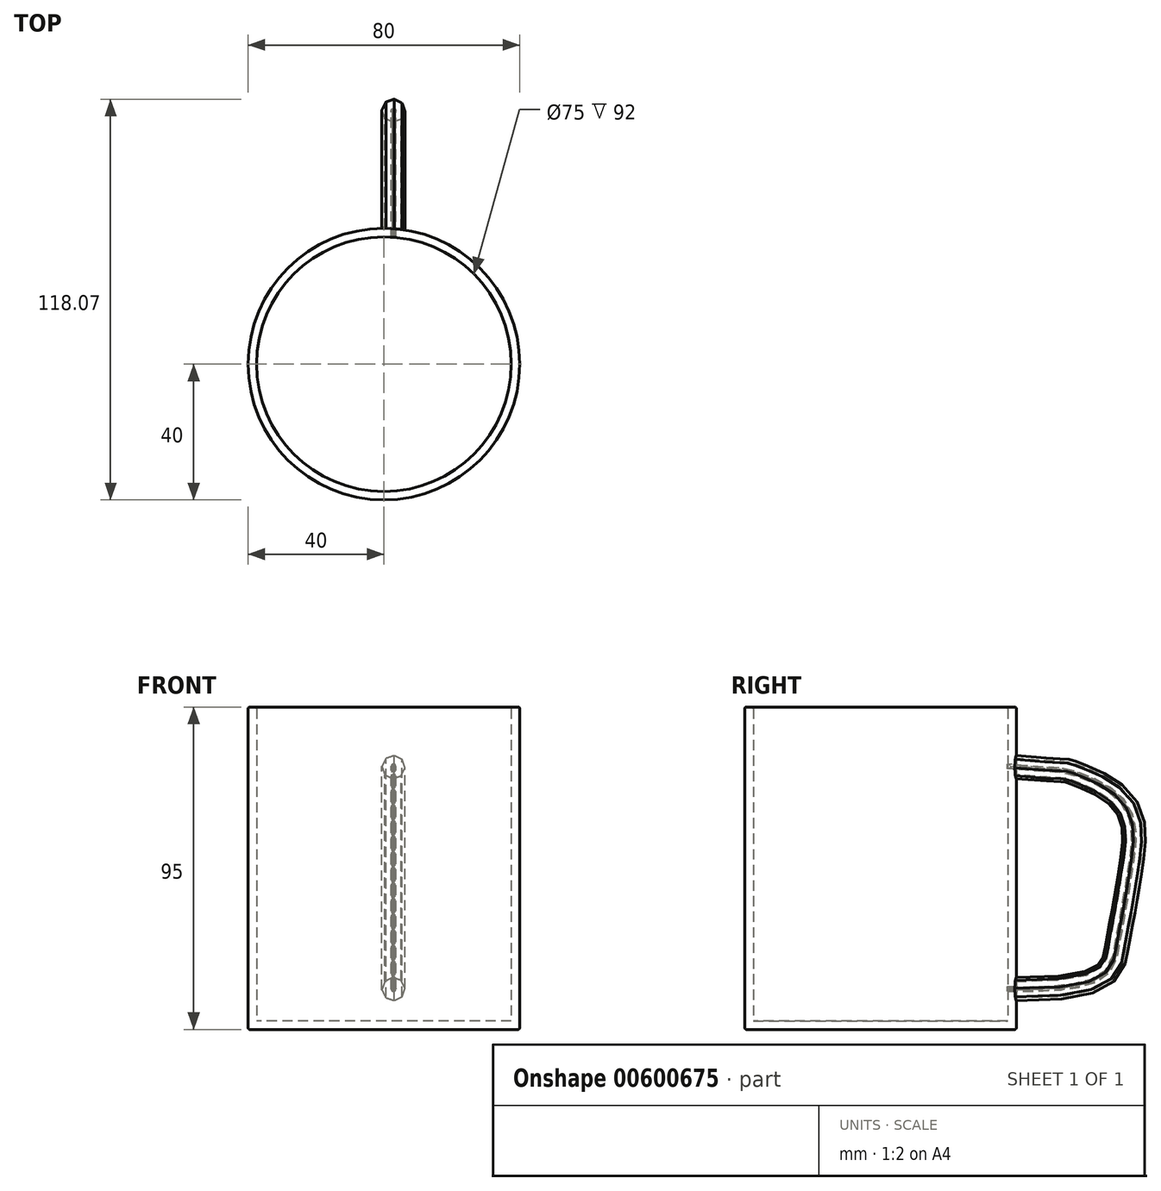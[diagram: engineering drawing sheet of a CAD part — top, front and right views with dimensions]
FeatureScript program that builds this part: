
annotation { "Feature Type Name" : "Feature", "Feature Type Description" : "" }
export const myFeature = defineFeature(function(context is Context, id is Id, definition is map)
    precondition{}
    {
        {
            var Q0;
            Q0=qCreatedBy(makeId("Top.planeOp"),FACE);
            var sketch = newSketch(context, id + "F0", { "sketchPlane" : qUnion([Q0])});
            skCircle(sketch, "E0", {"center": v(0, 0) * mm, "radius": 40 * mm});
            skSolve(sketch);
        }
        {
            var Q0;
            Q0 = qSketchRegion(id + "F0", true);
            extrude(context, id + "F1", {"entities" : qUnion([Q0]), "depth" : 95 * mm, "offsetDistance" : 25 * mm});
        }
        {
            var Q0;
            Q0=qCreatedBy(makeId("Right.planeOp"),FACE);
            var sketch = newSketch(context, id + "F2", { "sketchPlane" : qUnion([Q0])});
            skFitSpline(sketch, "E1", {"points": [v(34.46, 75.67) * mm, v(56.12, 73.65) * mm, v(70.16, 65.33) * mm, v(71.73, 48.66) * mm, v(69.62, 35.85) * mm, v(67.55, 24.47) * mm, v(35.43, 14.05) * mm], "startDerivative": vector(367.39, -34.48) * mm, "endDerivative": vector(-409.48, 9.9) * mm});
            skSolve(sketch);
        }
        {
            var Q0;
            Q0=qCreatedBy(makeId("Front.planeOp"),FACE);
            cPlane(context, id + "F3", {"entities" : qUnion([Q0]), "cplaneType" : CPlaneType.OFFSET, "offset" : 40 * mm, "oppositeDirection" : true, "width" : 150 * mm, "height" : 150 * mm});
        }
        {
            var Q0;
            Q0=qCreatedBy(id+"F3.planeOp",FACE);
            var sketch = newSketch(context, id + "F4", { "sketchPlane" : qUnion([Q0])});
            skCircle(sketch, "E2.cCircle", {"center": v(2.82, 77.26) * mm, "radius": 3.14 * mm, "construction": true});
            skLineSegment(sketch, "E2.0", {"start": v(-0.58, 77.5) * mm, "end": v(0.58, 79.82) * mm});
            skLineSegment(sketch, "E2.1", {"start": v(0.58, 79.82) * mm, "end": v(3.04, 80.66) * mm});
            skLineSegment(sketch, "E2.2", {"start": v(3.04, 80.66) * mm, "end": v(5.38, 79.5) * mm});
            skLineSegment(sketch, "E2.3", {"start": v(5.38, 79.5) * mm, "end": v(6.21, 77.04) * mm});
            skLineSegment(sketch, "E2.4", {"start": v(6.21, 77.04) * mm, "end": v(5.06, 74.7) * mm});
            skLineSegment(sketch, "E2.5", {"start": v(5.06, 74.7) * mm, "end": v(2.6, 73.87) * mm});
            skLineSegment(sketch, "E2.6", {"start": v(2.6, 73.87) * mm, "end": v(0.26, 75.02) * mm});
            skLineSegment(sketch, "E2.7", {"start": v(0.26, 75.02) * mm, "end": v(-0.58, 77.5) * mm});
            skPoint(sketch, "E2.0.midPoint", {"position": v(0, 78.66) * mm});
            skSolve(sketch);
        }
        {
            var Q0;
            Q0=makeQuery(id+"F4.imprint","IMPRINT",FACE,{"disambiguationData":[TD([[makeQuery(id+"F4.imprint","IMPRINT",EDGE,{"derivedFrom":sQuery(id+"F4.wireOp",EDGE,"E2.0")}),-1.0]])]});
            var Q1;
            Q1 = qConstructionFilter(qBodyType(qCreatedBy(id + "F2" ,EDGE), BodyType.WIRE), ConstructionObject.NO);
            sweep(context, id + "F5", {"operationType" : NewBodyOperationType.ADD, "profiles" : qUnion([Q0]), "path" : qUnion([Q1])});
        }
        {
            var Q0;
            Q0=makeQuery(id+"F1.opExtrude","CAP_FACE",FACE,{"disambiguationData":[OSD([sQuery(id+"F0.wireOp",EDGE,"E0")])],"isStart":false});
            shell(context, id + "F6", {"entities" : qUnion([Q0]), "thickness" : 2.5 * mm});
        }
        {
            var Q0;
            Q0=makeQuery(id+"F1.opExtrude","CAP_FACE",FACE,{"disambiguationData":[OSD([sQuery(id+"F0.wireOp",EDGE,"E0")])],"isStart":false});
            var Q1;
            Q1=makeQuery(id+"F1.opExtrude","CAP_EDGE",EDGE,{"disambiguationData":[OSD([sQuery(id+"F0.wireOp",EDGE,"E0")])],"isStart":true});
            fillet(context, id + "F7", {"entities" : qUnion([Q0, Q1]), "radius" : 0.5 * mm, "tangentPropagation" : true, "allowEdgeOverflow" : false});
        }
    });
